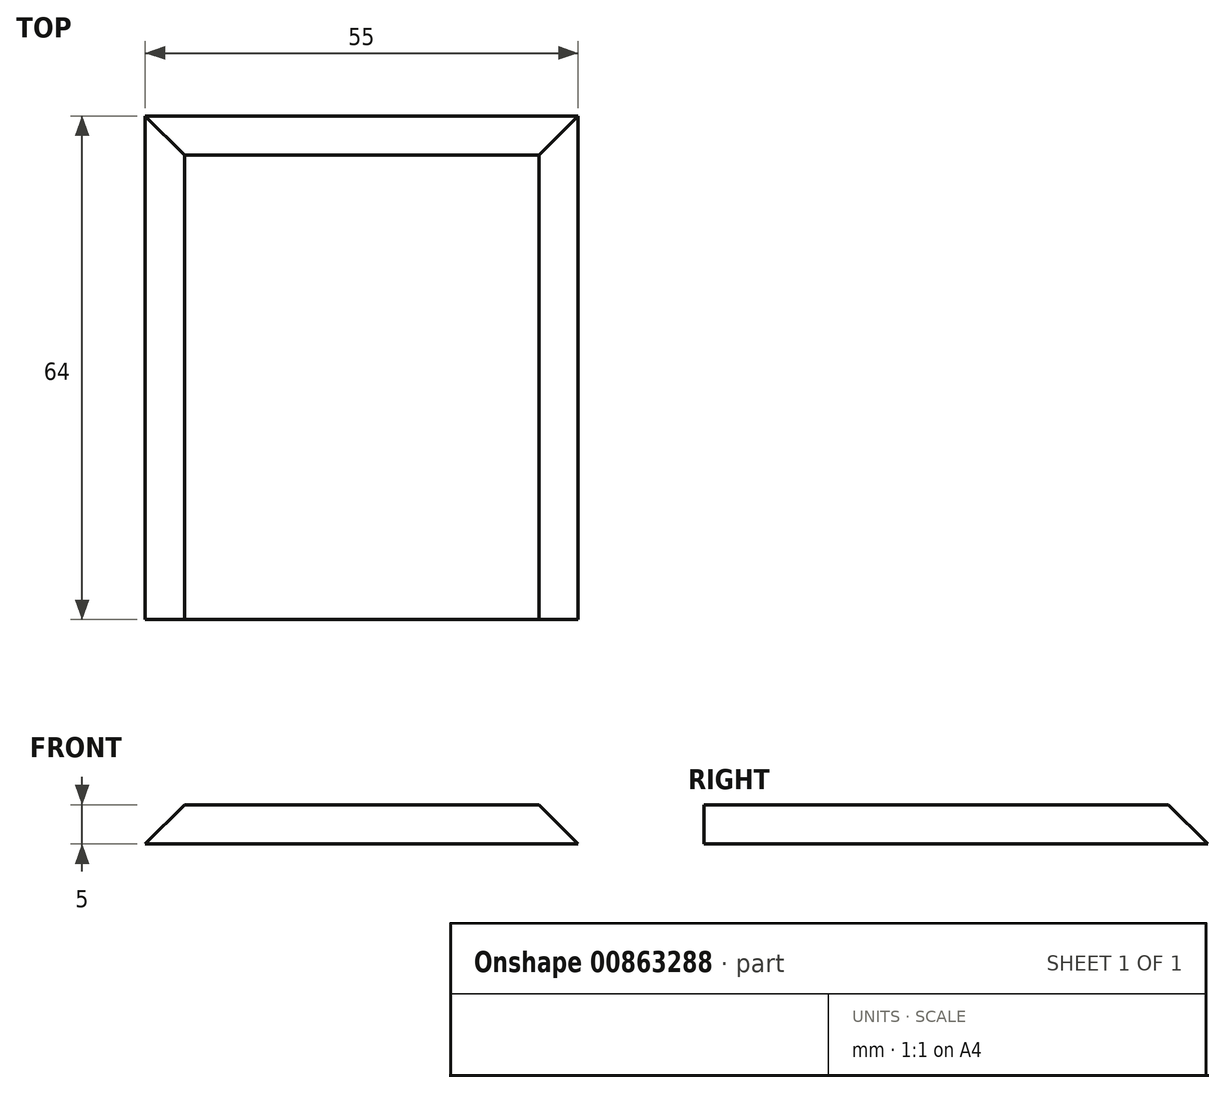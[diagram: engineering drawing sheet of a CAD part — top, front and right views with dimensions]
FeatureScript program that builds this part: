
annotation { "Feature Type Name" : "Feature", "Feature Type Description" : "" }
export const myFeature = defineFeature(function(context is Context, id is Id, definition is map)
    precondition{}
    {
        {
            var Q0;
            Q0=qCreatedBy(makeId("Top.planeOp"),FACE);
            var sketch = newSketch(context, id + "F0", { "sketchPlane" : qUnion([Q0])});
            skLineSegment(sketch, "E0.bottom", {"start": v(27.5, -52.5) * mm, "end": v(-27.5, -52.5) * mm});
            skLineSegment(sketch, "E0.top", {"start": v(27.5, 52.5) * mm, "end": v(-27.5, 52.5) * mm});
            skLineSegment(sketch, "E0.left", {"start": v(27.5, -52.5) * mm, "end": v(27.5, 52.5) * mm});
            skLineSegment(sketch, "E0.right", {"start": v(-27.5, -52.5) * mm, "end": v(-27.5, 52.5) * mm});
            skPoint(sketch, "E0.middle", {"position": v(0, 0) * mm});
            skLineSegment(sketch, "E1", {"start": v(27.5, -14.74) * mm, "end": v(-27.5, -11.5) * mm});
            skLineSegment(sketch, "E2", {"start": v(-27.5, -11.5) * mm, "end": v(27.5, -11.5) * mm});
            skSolve(sketch);
        }
        {
            var Q0;
            {var subQ0=sQuery(id+"F0.wireOp",EDGE,"E0.top");Q0=makeQuery(id+"F0.imprint","IMPRINT",FACE,{"disambiguationData":[TD([[makeQuery(id+"F0.imprint","IMPRINT",EDGE,{"derivedFrom":subQ0}),1.0]])]});}
            extrude(context, id + "F1", {"entities" : qUnion([Q0]), "depth" : 5 * mm, "offsetDistance" : 25 * mm});
        }
        {
            var Q0;
            Q0=makeQuery(id+"F1.opExtrude","CAP_EDGE",EDGE,{"disambiguationData":[OSD([sQuery(id+"F0.wireOp",EDGE,"E0.right")])],"isStart":false});
            var Q1;
            Q1=makeQuery(id+"F1.opExtrude","CAP_EDGE",EDGE,{"disambiguationData":[OSD([sQuery(id+"F0.wireOp",EDGE,"E0.top")])],"isStart":false});
            var Q2;
            Q2=makeQuery(id+"F1.opExtrude","CAP_EDGE",EDGE,{"disambiguationData":[OSD([sQuery(id+"F0.wireOp",EDGE,"E0.left")])],"isStart":false});
            chamfer(context, id + "F2", {"entities" : qUnion([Q0, Q1, Q2]), "width" : 5 * mm, "tangentPropagation" : true});
        }
    });
